# Revit family: BTKP-150X30-500-840-xxx-SWF
name_source: partatom
category: Oprawy oświetleniowe
revit_build: Autodesk Revit 2017 (Build: 20190507_1515(x64)
units: mm (PartAtom-declared; Revit-internal decimal feet)

## family parameters
Numer OmniClass = 23.80.70.11
Obiekt nadrzędny = Powierzchnia
Punkt obliczania pomieszczeń = Nie
Tnij formami wycięć po wczytaniu = Nie
Typ części = Normalny
Tytuł OmniClass = Luminaries for Internal Lighting
Współdzielony = Nie
Wymiar okrągłego złącza = Użyj średnicy
Źródło światła = Tak

## types (4) — shared parameters
Emituj kształt widoczny w renderingu = Nie
Emituj z długości prostokąta = 31 mm  [stored 0.101706 ft]
Emituj z szerokości prostokąta = 1498 mm  [stored 4.9147 ft]
Filtr koloru = 16777215
Kod zespołu = D5020200
Lampa = LED
Obciążenie pozorne = 33 VA
Odchylenie kierunku = 90.00°
Producent = RIDI Leuchten GmbH
URL = www.spectral.de
Zmiana temperatury barwowej przyciemniania lampy = <Brak>
brand = Spectral
conformity mark = CE
electrical safety class = 1
height = 300 mm
ingress protection (IP) code = IP20
length = 1500 mm  [stored 4.92126 ft]
nominal frequency = 50-60Hz
nominal voltage = 230
rated input power = 33
voltage type (AC, DC, UC) = AC
weight = 10.8 kg
width = 42 mm  [stored 0.137795 ft]
zero-valued in all types: Domyślna rzędna

## per-type parameters (varying)
| type | Model | Plik sieci fotometrycznej |
| BTKP 150X30/500-840 DPO-SWF | SPK0620026BL | BTKP 150x30500-840 DPO-SWF.IES |
| BTKP 150X30/500-840 DPO-DA-SWF | SPK0630026BL | BTKP 150x30500-840 DPO-SWF.IES |
| BTKP 150X30/500-840 MPS-SWF | SPK0620027BL | BTKP 150x30500-840 MPS-SWF.IES |
| BTKP 150X30/500-840 MPS-DA-SWF | SPK0630027BL | BTKP 150x30500-840 MPS-SWF.IES |

note: column(s) folded — value = type name in every type: product name

note: [stored X ft] marks values corroborated as IEEE doubles in the binary element streams (Revit-internal decimal feet)
